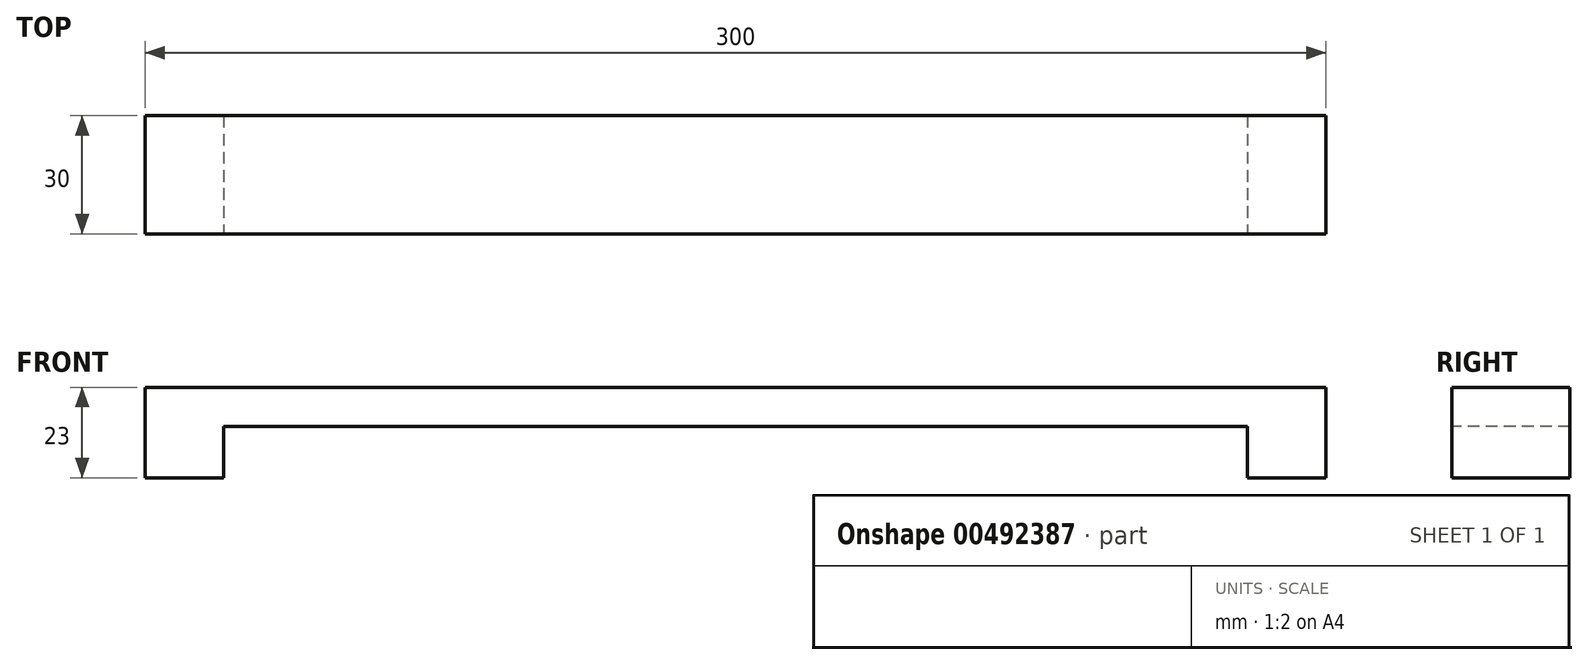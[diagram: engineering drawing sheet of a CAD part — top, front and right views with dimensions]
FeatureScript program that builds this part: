
annotation { "Feature Type Name" : "Feature", "Feature Type Description" : "" }
export const myFeature = defineFeature(function(context is Context, id is Id, definition is map)
    precondition{}
    {
        {
            var Q0;
            Q0=qCreatedBy(makeId("Top.planeOp"),FACE);
            var sketch = newSketch(context, id + "F0", { "sketchPlane" : qUnion([Q0])});
            skLineSegment(sketch, "E0.bottom", {"start": v(-150, 30) * mm, "end": v(-130, 30) * mm});
            skLineSegment(sketch, "E0.top", {"start": v(-150, 0) * mm, "end": v(-130, 0) * mm});
            skLineSegment(sketch, "E0.left", {"start": v(-150, 30) * mm, "end": v(-150, 0) * mm});
            skLineSegment(sketch, "E0.right", {"start": v(-130, 30) * mm, "end": v(-130, 0) * mm});
            skLineSegment(sketch, "E1.bottom", {"start": v(130, 30) * mm, "end": v(150, 30) * mm});
            skLineSegment(sketch, "E1.top", {"start": v(130, 0) * mm, "end": v(150, 0) * mm});
            skLineSegment(sketch, "E1.left", {"start": v(130, 30) * mm, "end": v(130, 0) * mm});
            skLineSegment(sketch, "E1.right", {"start": v(150, 30) * mm, "end": v(150, 0) * mm});
            skSolve(sketch);
        }
        {
            var Q0;
            Q0 = qSketchRegion(id + "F0", true);
            extrude(context, id + "F1", {"entities" : qUnion([Q0]), "depth" : 13 * mm, "offsetDistance" : 25 * mm});
        }
        {
            var Q0;
            Q0=makeQuery(id+"F1.opExtrude","CAP_FACE",FACE,{"disambiguationData":[OSD([sQuery(id+"F0.wireOp",EDGE,"E0.bottom"),sQuery(id+"F0.wireOp",EDGE,"E0.top"),sQuery(id+"F0.wireOp",EDGE,"E0.left"),sQuery(id+"F0.wireOp",EDGE,"E0.right")])],"isStart":false});
            var sketch = newSketch(context, id + "F2", { "sketchPlane" : qUnion([Q0])});
            skLineSegment(sketch, "E2.bottom", {"start": v(-150, 0) * mm, "end": v(150, 0) * mm});
            skLineSegment(sketch, "E2.top", {"start": v(-150, 30) * mm, "end": v(150, 30) * mm});
            skLineSegment(sketch, "E2.left", {"start": v(-150, 0) * mm, "end": v(-150, 30) * mm});
            skLineSegment(sketch, "E2.right", {"start": v(150, 0) * mm, "end": v(150, 30) * mm});
            skSolve(sketch);
        }
        {
            var Q0;
            Q0 = qSketchRegion(id + "F2", true);
            extrude(context, id + "F3", {"entities" : qUnion([Q0]), "operationType" : NewBodyOperationType.ADD, "depth" : 10 * mm});
        }
    });
